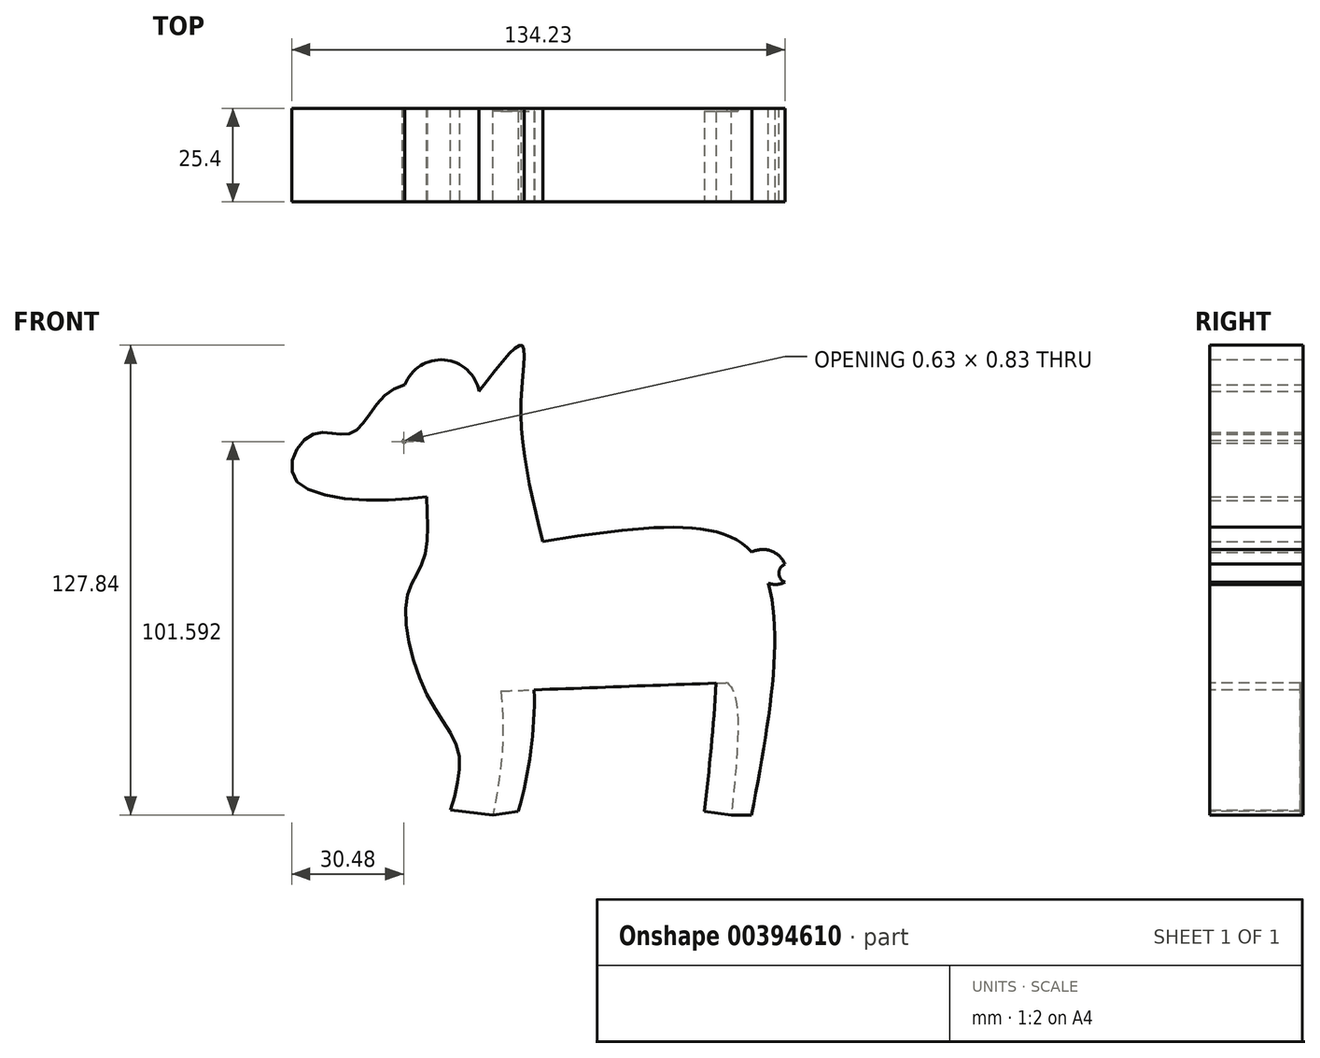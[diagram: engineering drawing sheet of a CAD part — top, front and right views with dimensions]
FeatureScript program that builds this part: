
annotation { "Feature Type Name" : "Feature", "Feature Type Description" : "" }
export const myFeature = defineFeature(function(context is Context, id is Id, definition is map)
    precondition{}
    {
        {
            var Q0;
            Q0=qCreatedBy(makeId("Front.planeOp"),FACE);
            var sketch = newSketch(context, id + "F0", { "sketchPlane" : qUnion([Q0])});
            skFitSpline(sketch, "E0", {"points": [v(-26.26, 37.92) * mm, v(-50.53, 37.92) * mm, v(-60.95, 26.54) * mm, v(-71.57, 26.16) * mm, v(-75.74, 13.27) * mm, v(-35.93, 10.62) * mm, v(-35.17, 12.7) * mm], "startDerivative": vector(-133.46, 27.93) * mm, "endDerivative": vector(-8.93, 34.08) * mm});
            skFitSpline(sketch, "E1", {"points": [v(-40.56, 9.28) * mm, v(-41.42, -7.96) * mm, v(-45.98, -18.4) * mm, v(-40.67, -44.18) * mm, v(-31.95, -60.1) * mm, v(-34.03, -76.03) * mm], "startDerivative": vector(5.05, -96.32) * mm, "endDerivative": vector(-25.04, -87.1) * mm});
            skFitSpline(sketch, "E2", {"points": [v(-26.26, 37.92) * mm, v(-14.7, 50.43) * mm, v(-14.88, 34.13) * mm, v(-8.44, -5.12) * mm], "startDerivative": vector(52.3, 69.4) * mm, "endDerivative": vector(23.01, -92.1) * mm});
            skFitSpline(sketch, "E3", {"points": [v(-22.28, -26.35) * mm, v(-19.81, -56.12) * mm, v(-22.47, -77.36) * mm], "startDerivative": vector(7.35, -57.3) * mm, "endDerivative": vector(-8.16, -44.34) * mm});
            skFitSpline(sketch, "E4", {"points": [v(-8.98, -2.93) * mm, v(44.08, -2.65) * mm, v(54.13, -27.11) * mm, v(47.88, -77.36) * mm], "startDerivative": vector(170.68, 26.54) * mm, "endDerivative": vector(-27.44, -145.77) * mm});
            skFitSpline(sketch, "E5", {"points": [v(31.57, -26.92) * mm, v(38.59, -39.06) * mm, v(42.95, -43.8) * mm, v(42.38, -77.36) * mm], "startDerivative": vector(22.18, -46.46) * mm, "endDerivative": vector(-8.92, -88.15) * mm});
            skFitSpline(sketch, "E6", {"points": [v(-20.3, -43.64) * mm, v(41.21, -41.37) * mm], "startDerivative": vector(61.53, 2.22) * mm, "endDerivative": vector(61.53, 2.22) * mm});
            skArc(sketch, "E7", {"start": v(56.95, -9.12) * mm, "mid": v(53.17, -5.5) * mm, "end": v(47.95, -5.84) * mm});
            skArc(sketch, "E8", {"start": v(56.95, -9.12) * mm, "mid": v(55.3, -11.58) * mm, "end": v(56.95, -14.03) * mm});
            skArc(sketch, "E9", {"start": v(48.9, -7) * mm, "mid": v(50.58, -13.2) * mm, "end": v(56.95, -14.03) * mm});
            skArc(sketch, "E10", {"start": v(-26.26, 37.92) * mm, "mid": v(-41.94, 45.04) * mm, "end": v(-43.32, 27.87) * mm});
            skArc(sketch, "E11", {"start": v(-47.11, 24.65) * mm, "mid": v(-43.12, 23.79) * mm, "end": v(-43.32, 27.87) * mm});
            skArc(sketch, "E12", {"start": v(-47.11, 24.65) * mm, "mid": v(-30.29, 21.23) * mm, "end": v(-26.26, 37.92) * mm});
            skFitSpline(sketch, "E13", {"points": [v(-34.03, -76.03) * mm, v(-22.47, -77.36) * mm], "startDerivative": vector(11.57, -1.33) * mm, "endDerivative": vector(11.57, -1.33) * mm});
            skFitSpline(sketch, "E14", {"points": [v(42.38, -77.36) * mm, v(47.88, -77.36) * mm], "startDerivative": vector(5.5, 0) * mm, "endDerivative": vector(5.5, 0) * mm});
            skSolve(sketch);
        }
        {
            var Q0;
            Q0 = qSketchRegion(id + "F0", true);
            extrude(context, id + "F1", {"entities" : qUnion([Q0]), "depth" : 25.4 * mm});
        }
        {
            var Q0;
            Q0=makeQuery(id+"F1.opExtrude","CAP_FACE",FACE,{"disambiguationData":[OSD([sQuery(id+"F0.wireOp",EDGE,"E0"),sQuery(id+"F0.wireOp",EDGE,"E1"),sQuery(id+"F0.wireOp",EDGE,"E2"),sQuery(id+"F0.wireOp",EDGE,"E3"),sQuery(id+"F0.wireOp",EDGE,"E4"),sQuery(id+"F0.wireOp",EDGE,"E5"),sQuery(id+"F0.wireOp",EDGE,"E6"),sQuery(id+"F0.wireOp",EDGE,"E7"),sQuery(id+"F0.wireOp",EDGE,"E8"),sQuery(id+"F0.wireOp",EDGE,"E9"),sQuery(id+"F0.wireOp",EDGE,"E10"),sQuery(id+"F0.wireOp",EDGE,"E11"),sQuery(id+"F0.wireOp",EDGE,"E12"),sQuery(id+"F0.wireOp",EDGE,"E13"),sQuery(id+"F0.wireOp",EDGE,"E14")])],"isStart":false});
            var sketch = newSketch(context, id + "F2", { "sketchPlane" : qUnion([Q0])});
            skArc(sketch, "E15", {"start": v(35, -76.42) * mm, "mid": v(36.9, -58.98) * mm, "end": v(38.2, -41.48) * mm});
            skArc(sketch, "E16", {"start": v(-15.63, -76.42) * mm, "mid": v(-12.19, -60.03) * mm, "end": v(-11.27, -43.3) * mm});
            skFitSpline(sketch, "E17", {"points": [v(-15.63, -76.42) * mm, v(-22.47, -77.36) * mm], "startDerivative": vector(-6.84, -0.94) * mm, "endDerivative": vector(-6.84, -0.94) * mm});
            skFitSpline(sketch, "E18", {"points": [v(35, -76.42) * mm, v(42.38, -77.36) * mm], "startDerivative": vector(7.38, -0.94) * mm, "endDerivative": vector(7.38, -0.94) * mm});
            skSolve(sketch);
        }
        {
            var Q0;
            Q0 = qSketchRegion(id + "F2", true);
            var Q1;
            {var subQ0=sQuery(id+"F2.wireOp",EDGE,"E16");Q1=makeQuery(id+"F2.imprint","IMPRINT",FACE,{"disambiguationData":[TD([[makeQuery(id+"F2.imprint","IMPRINT",EDGE,{"derivedFrom":subQ0}),1.0]])]});}
            var Q2;
            {var subQ0=sQuery(id+"F2.wireOp",EDGE,"E15");Q2=makeQuery(id+"F2.imprint","IMPRINT",FACE,{"disambiguationData":[TD([[makeQuery(id+"F2.imprint","IMPRINT",EDGE,{"derivedFrom":subQ0}),-1.0]])]});}
            extrude(context, id + "F3", {"entities" : qUnion([Q0, Q1, Q2]), "operationType" : NewBodyOperationType.ADD, "oppositeDirection" : true, "depth" : 24.64 * mm});
        }
    });
